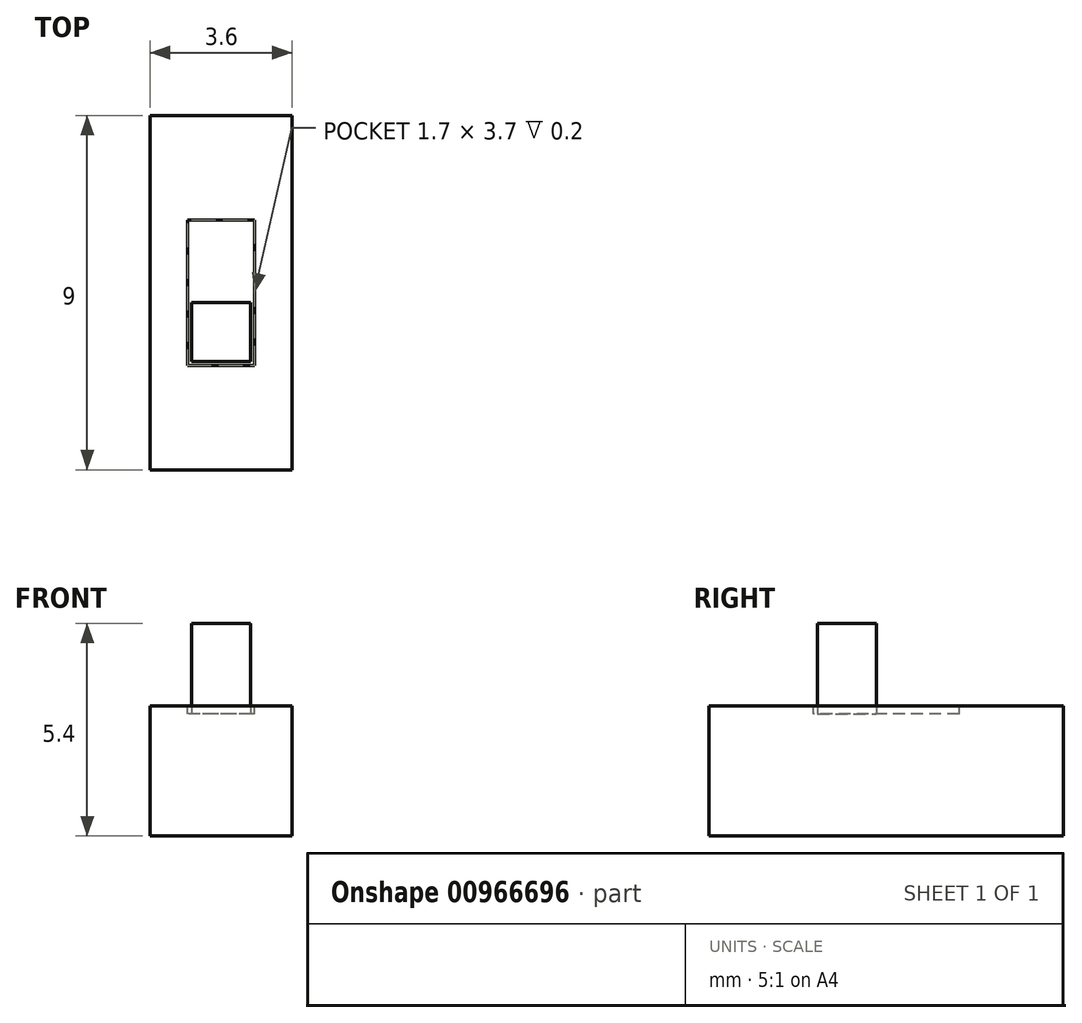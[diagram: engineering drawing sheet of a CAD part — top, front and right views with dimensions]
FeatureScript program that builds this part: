
annotation { "Feature Type Name" : "Feature", "Feature Type Description" : "" }
export const myFeature = defineFeature(function(context is Context, id is Id, definition is map)
    precondition{}
    {
        {
            var Q0;
            Q0=qCreatedBy(makeId("Top.planeOp"),FACE);
            var sketch = newSketch(context, id + "F0", { "sketchPlane" : qUnion([Q0])});
            skLineSegment(sketch, "E0.bottom", {"start": v(1.8, 4.5) * mm, "end": v(-1.8, 4.5) * mm});
            skLineSegment(sketch, "E0.top", {"start": v(1.8, -4.5) * mm, "end": v(-1.8, -4.5) * mm});
            skLineSegment(sketch, "E0.left", {"start": v(1.8, 4.5) * mm, "end": v(1.8, -4.5) * mm});
            skLineSegment(sketch, "E0.right", {"start": v(-1.8, 4.5) * mm, "end": v(-1.8, -4.5) * mm});
            skPoint(sketch, "E0.middle", {"position": v(0, 0) * mm});
            skSolve(sketch);
        }
        {
            var Q0;
            Q0 = qSketchRegion(id + "F0", true);
            extrude(context, id + "F1", {"entities" : qUnion([Q0]), "endBound" : BoundingType.SYMMETRIC, "depth" : 3.3 * mm, "offsetDistance" : 25 * mm});
        }
        {
            var Q0;
            Q0=makeQuery(id+"F1.opExtrude","CAP_FACE",FACE,{"disambiguationData":[OSD([sQuery(id+"F0.wireOp",EDGE,"E0.bottom"),sQuery(id+"F0.wireOp",EDGE,"E0.top"),sQuery(id+"F0.wireOp",EDGE,"E0.left"),sQuery(id+"F0.wireOp",EDGE,"E0.right")])],"isStart":false});
            var sketch = newSketch(context, id + "F2", { "sketchPlane" : qUnion([Q0])});
            skLineSegment(sketch, "E1.bottom", {"start": v(0.85, 1.85) * mm, "end": v(-0.85, 1.85) * mm});
            skLineSegment(sketch, "E1.top", {"start": v(0.85, -1.85) * mm, "end": v(-0.85, -1.85) * mm});
            skLineSegment(sketch, "E1.left", {"start": v(0.85, 1.85) * mm, "end": v(0.85, -1.85) * mm});
            skLineSegment(sketch, "E1.right", {"start": v(-0.85, 1.85) * mm, "end": v(-0.85, -1.85) * mm});
            skPoint(sketch, "E1.middle", {"position": v(0, 0) * mm});
            skSolve(sketch);
        }
        {
            var Q0;
            Q0 = qSketchRegion(id + "F2", true);
            extrude(context, id + "F3", {"entities" : qUnion([Q0]), "operationType" : NewBodyOperationType.REMOVE, "oppositeDirection" : true, "depth" : 0.2 * mm, "offsetDistance" : 25 * mm});
        }
        {
            var Q0;
            Q0=makeQuery(id+"F3.boolean.opBoolean","COPY",FACE,{"derivedFrom":makeQuery(id+"F3.opExtrude","CAP_FACE",FACE,{"disambiguationData":[OSD([sQuery(id+"F2.wireOp",EDGE,"E1.bottom"),sQuery(id+"F2.wireOp",EDGE,"E1.top"),sQuery(id+"F2.wireOp",EDGE,"E1.left"),sQuery(id+"F2.wireOp",EDGE,"E1.right")])],"isStart":false})});
            var sketch = newSketch(context, id + "F4", { "sketchPlane" : qUnion([Q0])});
            skLineSegment(sketch, "E2.bottom", {"start": v(0.75, -1.75) * mm, "end": v(-0.75, -1.75) * mm});
            skLineSegment(sketch, "E2.top", {"start": v(0.75, -0.25) * mm, "end": v(-0.75, -0.25) * mm});
            skLineSegment(sketch, "E2.left", {"start": v(0.75, -1.75) * mm, "end": v(0.75, -0.25) * mm});
            skLineSegment(sketch, "E2.right", {"start": v(-0.75, -1.75) * mm, "end": v(-0.75, -0.25) * mm});
            skPoint(sketch, "E2.middle", {"position": v(0, -1) * mm});
            skLineSegment(sketch, "E3", {"start": v(0, -1.75) * mm, "end": v(0, -1.85) * mm, "construction": true});
            skSolve(sketch);
        }
        {
            var Q0;
            Q0 = qSketchRegion(id + "F4", true);
            extrude(context, id + "F5", {"entities" : qUnion([Q0]), "depth" : 2.3 * mm, "offsetDistance" : 25 * mm});
        }
    });
